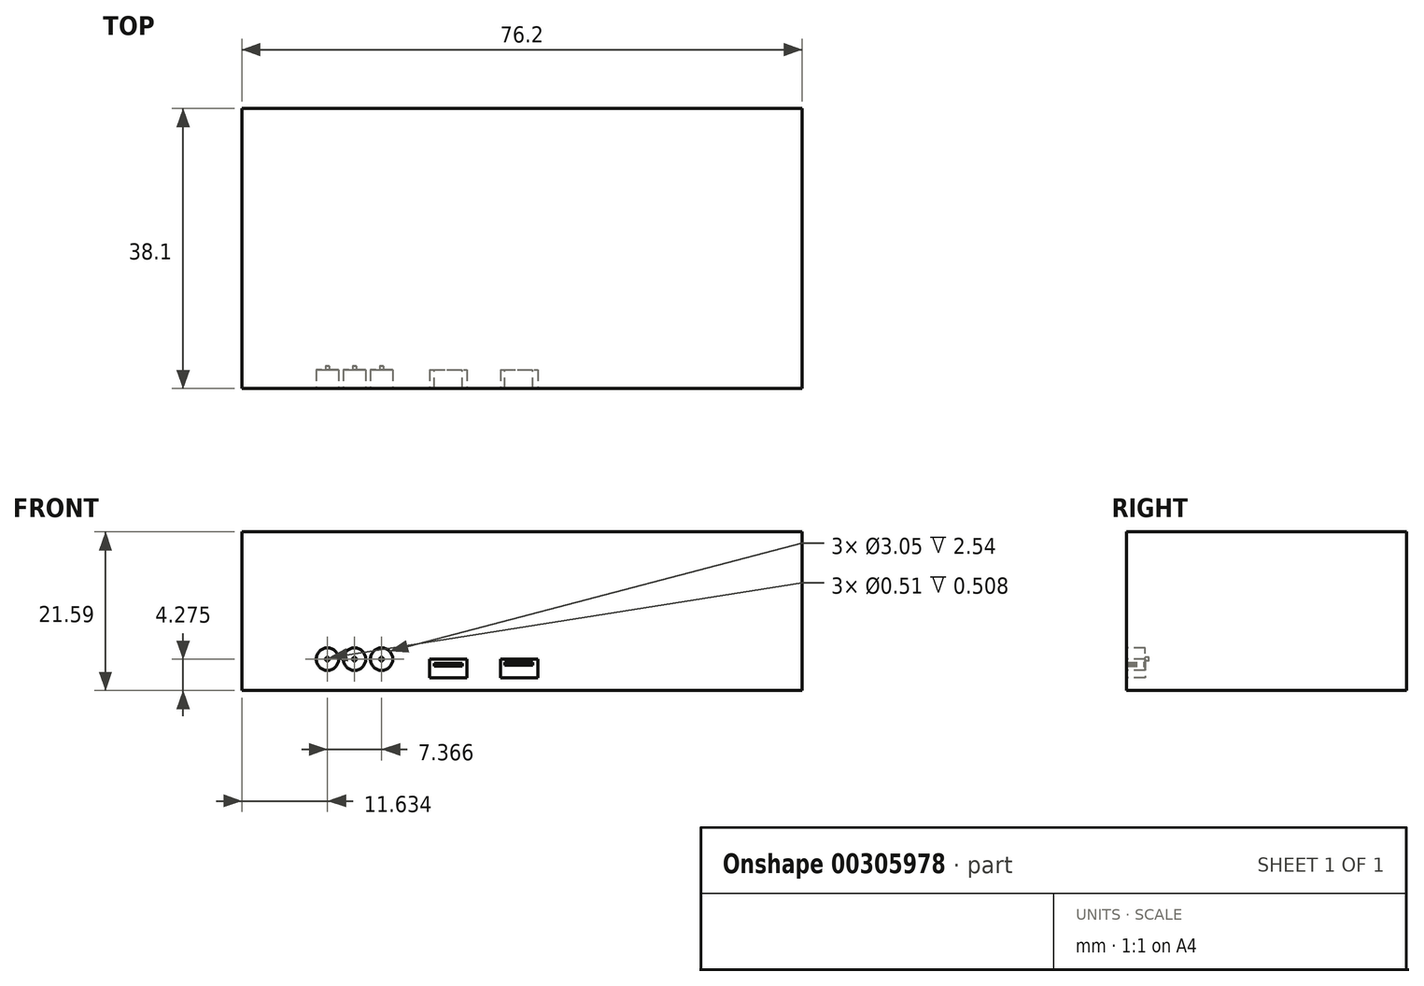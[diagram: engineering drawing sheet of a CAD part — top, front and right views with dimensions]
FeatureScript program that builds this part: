
annotation { "Feature Type Name" : "Feature", "Feature Type Description" : "" }
export const myFeature = defineFeature(function(context is Context, id is Id, definition is map)
    precondition{}
    {
        {
            var Q0;
            Q0=qCreatedBy(makeId("Front.planeOp"),FACE);
            var sketch = newSketch(context, id + "F0", { "sketchPlane" : qUnion([Q0])});
            skLineSegment(sketch, "E0.bottom", {"start": v(-57.56, 27.63) * mm, "end": v(18.64, 27.63) * mm});
            skLineSegment(sketch, "E0.top", {"start": v(-57.56, 6.04) * mm, "end": v(18.64, 6.04) * mm});
            skLineSegment(sketch, "E0.left", {"start": v(-57.56, 27.63) * mm, "end": v(-57.56, 6.04) * mm});
            skLineSegment(sketch, "E0.right", {"start": v(18.64, 27.63) * mm, "end": v(18.64, 6.04) * mm});
            skSolve(sketch);
        }
        {
            var Q0;
            Q0 = qSketchRegion(id + "F0", true);
            extrude(context, id + "F1", {"entities" : qUnion([Q0]), "depth" : 38.1 * mm});
        }
        {
            var Q0;
            Q0=makeQuery(id+"F1.opExtrude","CAP_FACE",FACE,{"disambiguationData":[OSD([sQuery(id+"F0.wireOp",EDGE,"E0.bottom"),sQuery(id+"F0.wireOp",EDGE,"E0.top"),sQuery(id+"F0.wireOp",EDGE,"E0.left"),sQuery(id+"F0.wireOp",EDGE,"E0.right")])],"isStart":false});
            var sketch = newSketch(context, id + "F2", { "sketchPlane" : qUnion([Q0])});
            skCircle(sketch, "E1", {"center": v(-45.93, 10.31) * mm, "radius": 1.52 * mm});
            skCircle(sketch, "E2", {"center": v(-42.24, 10.31) * mm, "radius": 1.52 * mm});
            skCircle(sketch, "E3", {"center": v(-38.56, 10.31) * mm, "radius": 1.52 * mm});
            skLineSegment(sketch, "E4.bottom", {"start": v(-32.01, 10.31) * mm, "end": v(-26.93, 10.31) * mm});
            skLineSegment(sketch, "E4.top", {"start": v(-32.01, 7.77) * mm, "end": v(-26.93, 7.77) * mm});
            skLineSegment(sketch, "E4.left", {"start": v(-32.01, 10.31) * mm, "end": v(-32.01, 7.77) * mm});
            skLineSegment(sketch, "E4.right", {"start": v(-26.93, 10.31) * mm, "end": v(-26.93, 7.77) * mm});
            skLineSegment(sketch, "E5.bottom", {"start": v(-22.4, 10.31) * mm, "end": v(-17.33, 10.31) * mm});
            skLineSegment(sketch, "E5.top", {"start": v(-22.4, 7.77) * mm, "end": v(-17.33, 7.77) * mm});
            skLineSegment(sketch, "E5.left", {"start": v(-22.4, 10.31) * mm, "end": v(-22.4, 7.77) * mm});
            skLineSegment(sketch, "E5.right", {"start": v(-17.33, 10.31) * mm, "end": v(-17.33, 7.77) * mm});
            skSolve(sketch);
        }
        {
            var Q0;
            Q0=makeQuery(id+"F2.imprint","IMPRINT",FACE,{"disambiguationData":[TD([[makeQuery(id+"F2.imprint","IMPRINT",EDGE,{"derivedFrom":sQuery(id+"F2.wireOp",EDGE,"E5.bottom")}),-1.0]])]});
            var Q1;
            Q1=makeQuery(id+"F2.imprint","IMPRINT",FACE,{"disambiguationData":[TD([[makeQuery(id+"F2.imprint","IMPRINT",EDGE,{"derivedFrom":sQuery(id+"F2.wireOp",EDGE,"E4.bottom")}),-1.0]])]});
            var Q2;
            Q2=makeQuery(id+"F2.imprint","IMPRINT",FACE,{"disambiguationData":[TD([[makeQuery(id+"F2.imprint","IMPRINT",EDGE,{"derivedFrom":sQuery(id+"F2.wireOp",EDGE,"E3")}),1.0]])]});
            var Q3;
            Q3=makeQuery(id+"F2.imprint","IMPRINT",FACE,{"disambiguationData":[TD([[makeQuery(id+"F2.imprint","IMPRINT",EDGE,{"derivedFrom":sQuery(id+"F2.wireOp",EDGE,"E2")}),1.0]])]});
            var Q4;
            Q4=makeQuery(id+"F2.imprint","IMPRINT",FACE,{"disambiguationData":[TD([[makeQuery(id+"F2.imprint","IMPRINT",EDGE,{"derivedFrom":sQuery(id+"F2.wireOp",EDGE,"E1")}),1.0]])]});
            extrude(context, id + "F3", {"entities" : qUnion([Q0, Q1, Q2, Q3, Q4]), "operationType" : NewBodyOperationType.REMOVE, "oppositeDirection" : true, "depth" : 2.54 * mm});
        }
        {
            var Q0;
            Q0=makeQuery(id+"F3.boolean.opBoolean","COPY",FACE,{"derivedFrom":makeQuery(id+"F3.opExtrude","CAP_FACE",FACE,{"disambiguationData":[OSD([sQuery(id+"F2.wireOp",EDGE,"E2")])],"isStart":false})});
            var sketch = newSketch(context, id + "F4", { "sketchPlane" : qUnion([Q0])});
            skCircle(sketch, "E6", {"center": v(-42.24, 10.31) * mm, "radius": 0.25 * mm});
            skSolve(sketch);
        }
        {
            var Q0;
            Q0 = qSketchRegion(id + "F4", true);
            extrude(context, id + "F5", {"entities" : qUnion([Q0]), "operationType" : NewBodyOperationType.REMOVE, "oppositeDirection" : true, "depth" : 0.5 * mm});
        }
        {
            var Q0;
            Q0=makeQuery(id+"F3.boolean.opBoolean","COPY",FACE,{"derivedFrom":makeQuery(id+"F3.opExtrude","CAP_FACE",FACE,{"disambiguationData":[OSD([sQuery(id+"F2.wireOp",EDGE,"E3")])],"isStart":false})});
            var sketch = newSketch(context, id + "F6", { "sketchPlane" : qUnion([Q0])});
            skCircle(sketch, "E7", {"center": v(-38.56, 10.31) * mm, "radius": 0.25 * mm});
            skSolve(sketch);
        }
        {
            var Q0;
            Q0 = qSketchRegion(id + "F6", true);
            extrude(context, id + "F7", {"entities" : qUnion([Q0]), "operationType" : NewBodyOperationType.REMOVE, "oppositeDirection" : true, "depth" : 0.5 * mm});
        }
        {
            var Q0;
            Q0=makeQuery(id+"F3.boolean.opBoolean","COPY",FACE,{"derivedFrom":makeQuery(id+"F3.opExtrude","CAP_FACE",FACE,{"disambiguationData":[OSD([sQuery(id+"F2.wireOp",EDGE,"E1")])],"isStart":false})});
            var sketch = newSketch(context, id + "F8", { "sketchPlane" : qUnion([Q0])});
            skCircle(sketch, "E8", {"center": v(-45.93, 10.31) * mm, "radius": 0.25 * mm});
            skSolve(sketch);
        }
        {
            var Q0;
            Q0 = qSketchRegion(id + "F8", true);
            extrude(context, id + "F9", {"entities" : qUnion([Q0]), "operationType" : NewBodyOperationType.REMOVE, "oppositeDirection" : true, "depth" : 0.5 * mm});
        }
        {
            var Q0;
            Q0=makeQuery(id+"F3.boolean.opBoolean","COPY",FACE,{"derivedFrom":makeQuery(id+"F3.opExtrude","CAP_FACE",FACE,{"disambiguationData":[OSD([sQuery(id+"F2.wireOp",EDGE,"E4.bottom"),sQuery(id+"F2.wireOp",EDGE,"E4.top"),sQuery(id+"F2.wireOp",EDGE,"E4.left"),sQuery(id+"F2.wireOp",EDGE,"E4.right")])],"isStart":false})});
            var sketch = newSketch(context, id + "F10", { "sketchPlane" : qUnion([Q0])});
            skLineSegment(sketch, "E9.bottom", {"start": v(-31.42, 9.74) * mm, "end": v(-27.61, 9.74) * mm});
            skLineSegment(sketch, "E9.top", {"start": v(-31.42, 9.36) * mm, "end": v(-27.61, 9.36) * mm});
            skLineSegment(sketch, "E9.left", {"start": v(-31.42, 9.74) * mm, "end": v(-31.42, 9.36) * mm});
            skLineSegment(sketch, "E9.right", {"start": v(-27.61, 9.74) * mm, "end": v(-27.61, 9.36) * mm});
            skSolve(sketch);
        }
        {
            var Q0;
            Q0 = qSketchRegion(id + "F10", true);
            var Q1;
            Q1=makeQuery(id+"F1.opExtrude","CAP_FACE",FACE,{"disambiguationData":[OSD([sQuery(id+"F0.wireOp",EDGE,"E0.bottom"),sQuery(id+"F0.wireOp",EDGE,"E0.top"),sQuery(id+"F0.wireOp",EDGE,"E0.left"),sQuery(id+"F0.wireOp",EDGE,"E0.right")])],"isStart":false});
            extrude(context, id + "F11", {"entities" : qUnion([Q0]), "operationType" : NewBodyOperationType.ADD, "endBound" : BoundingType.UP_TO_SURFACE, "endBoundEntityFace" : qUnion([Q1]), "depth" : 1.27 * mm});
        }
        {
            var Q0;
            Q0=makeQuery(id+"F3.boolean.opBoolean","COPY",FACE,{"derivedFrom":makeQuery(id+"F3.opExtrude","CAP_FACE",FACE,{"disambiguationData":[OSD([sQuery(id+"F2.wireOp",EDGE,"E5.bottom"),sQuery(id+"F2.wireOp",EDGE,"E5.top"),sQuery(id+"F2.wireOp",EDGE,"E5.left"),sQuery(id+"F2.wireOp",EDGE,"E5.right")])],"isStart":false})});
            var sketch = newSketch(context, id + "F12", { "sketchPlane" : qUnion([Q0])});
            skLineSegment(sketch, "E10.bottom", {"start": v(-21.83, 9.85) * mm, "end": v(-18.02, 9.85) * mm});
            skLineSegment(sketch, "E10.top", {"start": v(-21.83, 9.47) * mm, "end": v(-18.02, 9.47) * mm});
            skLineSegment(sketch, "E10.left", {"start": v(-21.83, 9.85) * mm, "end": v(-21.83, 9.47) * mm});
            skLineSegment(sketch, "E10.right", {"start": v(-18.02, 9.85) * mm, "end": v(-18.02, 9.47) * mm});
            skSolve(sketch);
        }
        {
            var Q0;
            Q0 = qSketchRegion(id + "F12", true);
            var Q1;
            Q1=makeQuery(id+"F1.opExtrude","CAP_FACE",FACE,{"disambiguationData":[OSD([sQuery(id+"F0.wireOp",EDGE,"E0.bottom"),sQuery(id+"F0.wireOp",EDGE,"E0.top"),sQuery(id+"F0.wireOp",EDGE,"E0.left"),sQuery(id+"F0.wireOp",EDGE,"E0.right")])],"isStart":false});
            extrude(context, id + "F13", {"entities" : qUnion([Q0]), "operationType" : NewBodyOperationType.ADD, "endBound" : BoundingType.UP_TO_SURFACE, "endBoundEntityFace" : qUnion([Q1]), "depth" : 25.4 * mm});
        }
    });
